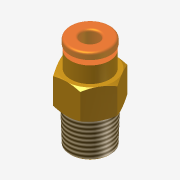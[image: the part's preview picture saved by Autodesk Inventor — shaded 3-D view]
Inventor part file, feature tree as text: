
AUTODESK INVENTOR PART (.ipt)
format: ipt  version: unknown  size: 242,176 bytes
history: native  units: in
note: dims shown in document units (in); Inventor stores cm internally (conversion verified against a paired STEP export)
features: imported_body x1, thread x1
ambient origin geometry x8: Origin, YZ Plane, XZ Plane, XY Plane, X Axis, Y Axis, Z Axis, Center Point
feature tree (2):
  imported_body  "Base1"
  thread  "Thread1"  [1 undecoded]
note: 1 required parameter value undecoded (feature->parameter linkage not recoverable at this tier; creation-order binding heuristic only, values carry confidence <= 0.55)
